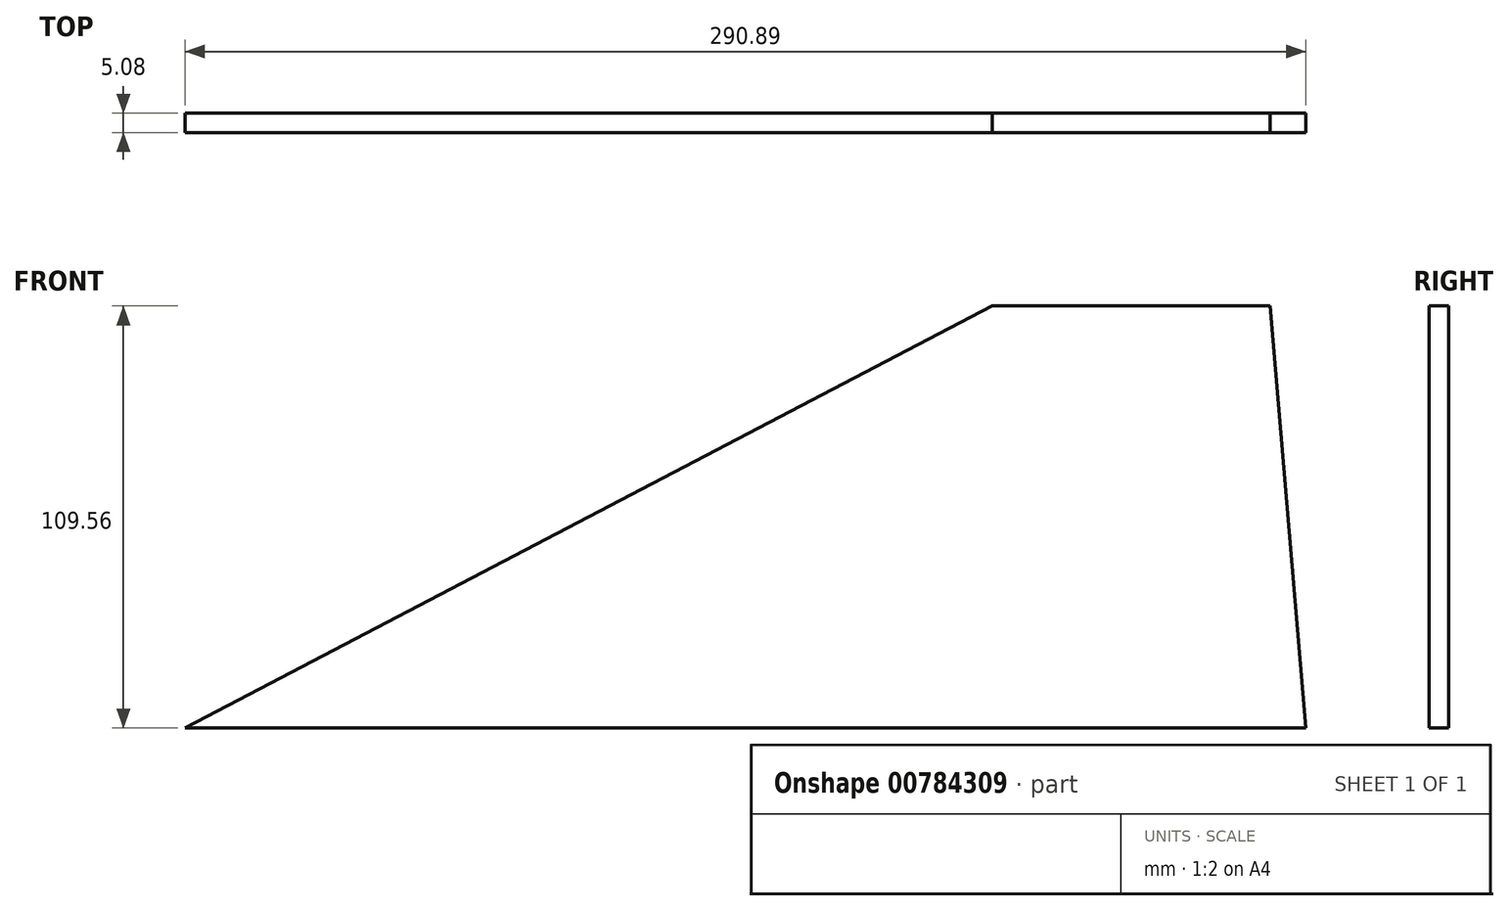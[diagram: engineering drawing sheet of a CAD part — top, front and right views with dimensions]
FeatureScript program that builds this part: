
annotation { "Feature Type Name" : "Feature", "Feature Type Description" : "" }
export const myFeature = defineFeature(function(context is Context, id is Id, definition is map)
    precondition{}
    {
        {
            var Q0;
            Q0=qCreatedBy(makeId("Front.planeOp"),FACE);
            var sketch = newSketch(context, id + "F0", { "sketchPlane" : qUnion([Q0])});
            skLineSegment(sketch, "E0", {"start": v(0, 0) * mm, "end": v(209.5, 109.56) * mm});
            skLineSegment(sketch, "E1", {"start": v(209.5, 109.56) * mm, "end": v(281.64, 109.56) * mm});
            skLineSegment(sketch, "E2", {"start": v(281.64, 109.56) * mm, "end": v(290.9, 0) * mm});
            skLineSegment(sketch, "E3", {"start": v(290.9, 0) * mm, "end": v(0, 0) * mm});
            skSolve(sketch);
        }
        {
            var Q0;
            Q0=makeQuery(id+"F0.imprint","IMPRINT",FACE,{"disambiguationData":[TD([[makeQuery(id+"F0.imprint","IMPRINT",EDGE,{"derivedFrom":sQuery(id+"F0.wireOp",EDGE,"E0")}),-1.0]])]});
            extrude(context, id + "F1", {"entities" : qUnion([Q0]), "depth" : 5.08 * mm, "offsetDistance" : 25.4 * mm});
        }
    });
